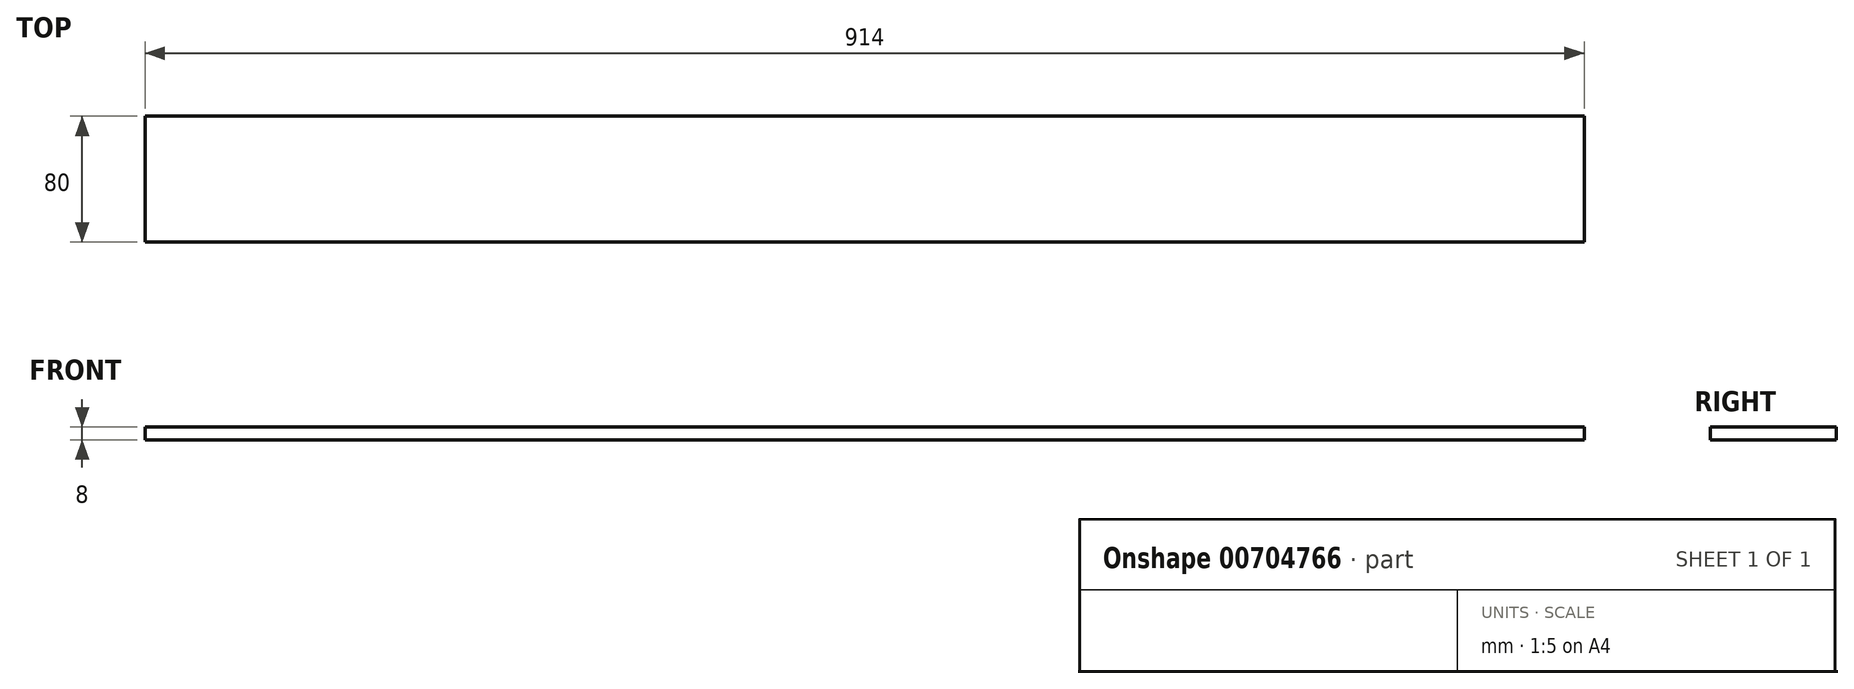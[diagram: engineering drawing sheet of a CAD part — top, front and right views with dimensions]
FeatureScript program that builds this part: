
annotation { "Feature Type Name" : "Feature", "Feature Type Description" : "" }
export const myFeature = defineFeature(function(context is Context, id is Id, definition is map)
    precondition{}
    {
        {
            var Q0;
            Q0=qCreatedBy(makeId("Top.planeOp"),FACE);
            var sketch = newSketch(context, id + "F0", { "sketchPlane" : qUnion([Q0])});
            skLineSegment(sketch, "E0.bottom", {"start": v(0, 0) * mm, "end": v(914, 0) * mm});
            skLineSegment(sketch, "E0.top", {"start": v(0, 80) * mm, "end": v(914, 80) * mm});
            skLineSegment(sketch, "E0.left", {"start": v(0, 0) * mm, "end": v(0, 80) * mm});
            skLineSegment(sketch, "E0.right", {"start": v(914, 0) * mm, "end": v(914, 80) * mm});
            skSolve(sketch);
        }
        {
            var Q0;
            Q0=makeQuery(id+"F0.imprint","IMPRINT",FACE,{"disambiguationData":[TD([[makeQuery(id+"F0.imprint","IMPRINT",EDGE,{"derivedFrom":sQuery(id+"F0.wireOp",EDGE,"E0.bottom")}),1.0]])]});
            extrude(context, id + "F1", {"entities" : qUnion([Q0]), "depth" : 8 * mm, "offsetDistance" : 25 * mm});
        }
    });
